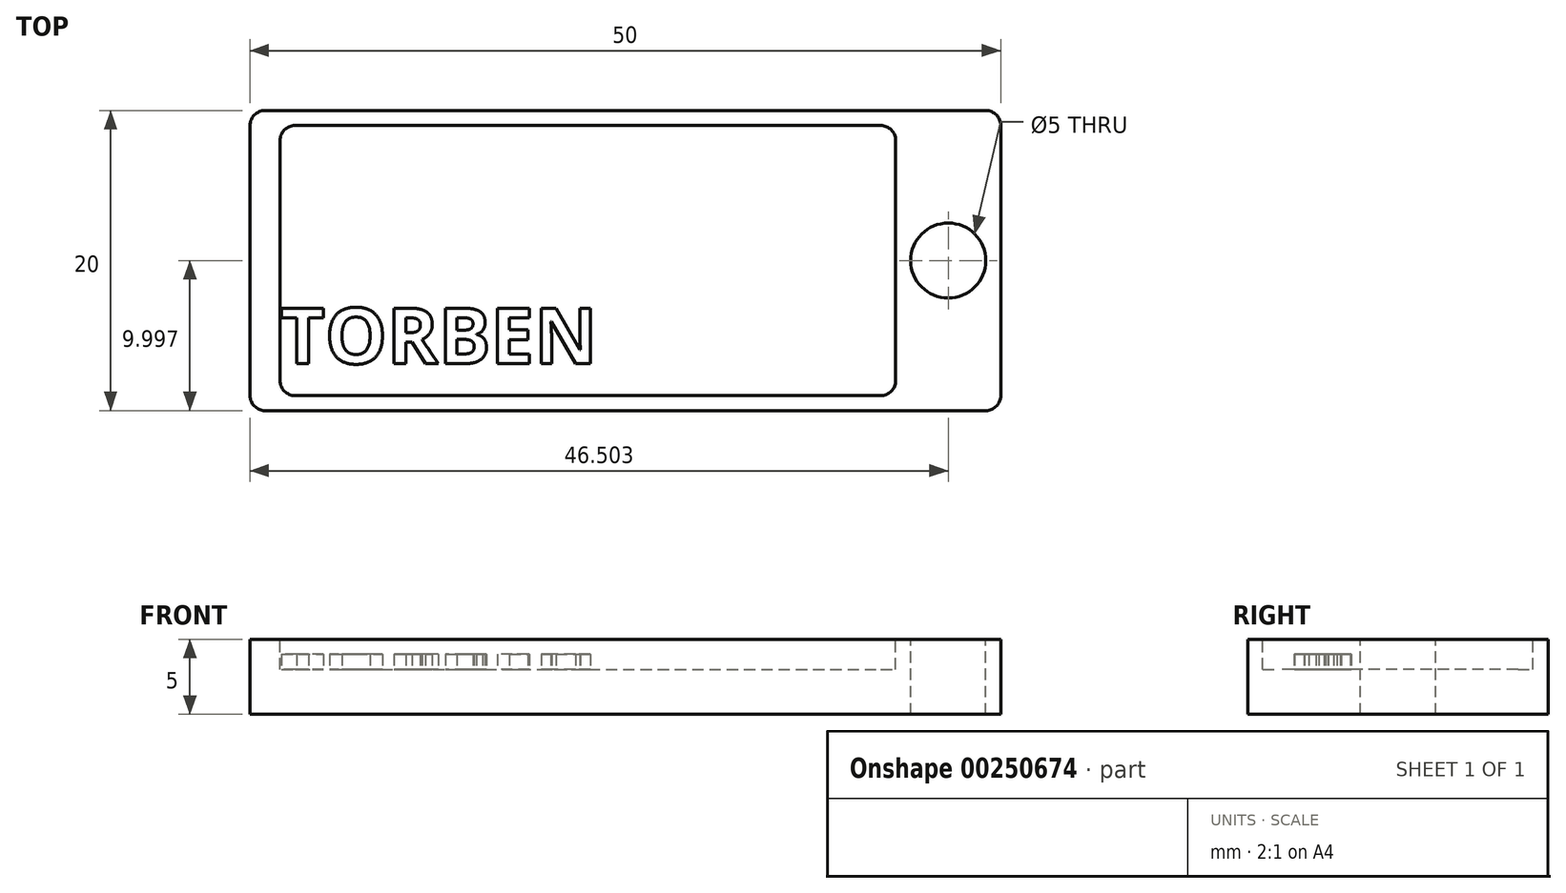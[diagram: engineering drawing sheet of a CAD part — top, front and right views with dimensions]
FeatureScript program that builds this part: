
annotation { "Feature Type Name" : "Feature", "Feature Type Description" : "" }
export const myFeature = defineFeature(function(context is Context, id is Id, definition is map)
    precondition{}
    {
        {
            var Q0;
            Q0=qCreatedBy(makeId("Top.planeOp"),FACE);
            var sketch = newSketch(context, id + "F0", { "sketchPlane" : qUnion([Q0])});
            skLineSegment(sketch, "E0.bottom", {"start": v(-8.37, 9.04) * mm, "end": v(41.63, 9.04) * mm});
            skLineSegment(sketch, "E0.top", {"start": v(-8.37, -10.96) * mm, "end": v(41.63, -10.96) * mm});
            skLineSegment(sketch, "E0.left", {"start": v(-8.37, 9.04) * mm, "end": v(-8.37, -10.96) * mm});
            skLineSegment(sketch, "E0.right", {"start": v(41.63, 9.04) * mm, "end": v(41.63, -10.96) * mm});
            skSolve(sketch);
        }
        {
            var Q0;
            Q0 = qSketchRegion(id + "F0", true);
            extrude(context, id + "F1", {"entities" : qUnion([Q0]), "depth" : 5 * mm});
        }
        {
            var Q0;
            Q0=makeQuery(id+"F1.opExtrude","CAP_FACE",FACE,{"disambiguationData":[OSD([sQuery(id+"F0.wireOp",EDGE,"E0.bottom"),sQuery(id+"F0.wireOp",EDGE,"E0.top"),sQuery(id+"F0.wireOp",EDGE,"E0.left"),sQuery(id+"F0.wireOp",EDGE,"E0.right")])],"isStart":false});
            var sketch = newSketch(context, id + "F2", { "sketchPlane" : qUnion([Q0])});
            skLineSegment(sketch, "E1.bottom", {"start": v(-6.37, 8.04) * mm, "end": v(34.63, 8.04) * mm});
            skLineSegment(sketch, "E1.top", {"start": v(-6.37, -9.96) * mm, "end": v(34.63, -9.96) * mm});
            skLineSegment(sketch, "E1.left", {"start": v(-6.37, 8.04) * mm, "end": v(-6.37, -9.96) * mm});
            skLineSegment(sketch, "E1.right", {"start": v(34.63, 8.04) * mm, "end": v(34.63, -9.96) * mm});
            skSolve(sketch);
        }
        {
            var Q0;
            Q0 = qSketchRegion(id + "F2", true);
            extrude(context, id + "F3", {"entities" : qUnion([Q0]), "operationType" : NewBodyOperationType.REMOVE, "oppositeDirection" : true, "depth" : 2 * mm});
        }
        {
            var Q0;
            Q0=makeQuery(id+"F1.opExtrude","SWEPT_EDGE",EDGE,{"disambiguationData":[OSD([sQuery(id+"F0.wireOp",EDGE,"E0.top"),sQuery(id+"F0.wireOp",EDGE,"E0.left")])]});
            var Q1;
            Q1=makeQuery(id+"F1.opExtrude","SWEPT_EDGE",EDGE,{"disambiguationData":[OSD([sQuery(id+"F0.wireOp",EDGE,"E0.bottom"),sQuery(id+"F0.wireOp",EDGE,"E0.left")])]});
            var Q2;
            Q2=makeQuery(id+"F1.opExtrude","SWEPT_EDGE",EDGE,{"disambiguationData":[OSD([sQuery(id+"F0.wireOp",EDGE,"E0.top"),sQuery(id+"F0.wireOp",EDGE,"E0.right")])]});
            var Q3;
            Q3=makeQuery(id+"F1.opExtrude","SWEPT_EDGE",EDGE,{"disambiguationData":[OSD([sQuery(id+"F0.wireOp",EDGE,"E0.bottom"),sQuery(id+"F0.wireOp",EDGE,"E0.right")])]});
            fillet(context, id + "F4", {"entities" : qUnion([Q0, Q1, Q2, Q3]), "radius" : 1 * mm, "tangentPropagation" : true, "allowEdgeOverflow" : false});
        }
        {
            var Q0;
            Q0=makeQuery(id+"F3.boolean.opBoolean","COPY",EDGE,{"derivedFrom":makeQuery(id+"F3.opExtrude","SWEPT_EDGE",EDGE,{"disambiguationData":[OSD([sQuery(id+"F2.wireOp",EDGE,"E1.bottom"),sQuery(id+"F2.wireOp",EDGE,"E1.left")])]})});
            var Q1;
            Q1=makeQuery(id+"F3.boolean.opBoolean","COPY",EDGE,{"derivedFrom":makeQuery(id+"F3.opExtrude","SWEPT_EDGE",EDGE,{"disambiguationData":[OSD([sQuery(id+"F2.wireOp",EDGE,"E1.bottom"),sQuery(id+"F2.wireOp",EDGE,"E1.right")])]})});
            var Q2;
            Q2=makeQuery(id+"F3.boolean.opBoolean","COPY",EDGE,{"derivedFrom":makeQuery(id+"F3.opExtrude","SWEPT_EDGE",EDGE,{"disambiguationData":[OSD([sQuery(id+"F2.wireOp",EDGE,"E1.top"),sQuery(id+"F2.wireOp",EDGE,"E1.left")])]})});
            var Q3;
            Q3=makeQuery(id+"F3.boolean.opBoolean","COPY",EDGE,{"derivedFrom":makeQuery(id+"F3.opExtrude","SWEPT_EDGE",EDGE,{"disambiguationData":[OSD([sQuery(id+"F2.wireOp",EDGE,"E1.top"),sQuery(id+"F2.wireOp",EDGE,"E1.right")])]})});
            fillet(context, id + "F5", {"entities" : qUnion([Q0, Q1, Q2, Q3]), "radius" : 1 * mm, "tangentPropagation" : true, "allowEdgeOverflow" : false});
        }
        {
            var Q0;
            Q0=makeQuery(id+"F1.opExtrude","CAP_FACE",FACE,{"disambiguationData":[OSD([sQuery(id+"F0.wireOp",EDGE,"E0.bottom"),sQuery(id+"F0.wireOp",EDGE,"E0.top"),sQuery(id+"F0.wireOp",EDGE,"E0.left"),sQuery(id+"F0.wireOp",EDGE,"E0.right")])],"isStart":false});
            var sketch = newSketch(context, id + "F6", { "sketchPlane" : qUnion([Q0])});
            skPoint(sketch, "E2", {"position": v(34.63, -0.96) * mm});
            skPoint(sketch, "E3", {"position": v(41.63, -0.96) * mm});
            skLineSegment(sketch, "E4", {"start": v(34.63, -0.96) * mm, "end": v(41.63, -0.96) * mm, "construction": true});
            skPoint(sketch, "E5", {"position": v(38.13, -0.96) * mm});
            skCircle(sketch, "E6", {"center": v(38.13, -0.96) * mm, "radius": 2.5 * mm});
            skSolve(sketch);
        }
        {
            var Q0;
            Q0 = qSketchRegion(id + "F6", true);
            extrude(context, id + "F7", {"entities" : qUnion([Q0]), "operationType" : NewBodyOperationType.REMOVE, "oppositeDirection" : true, "depth" : 25 * mm});
        }
        {
            var Q0;
            Q0=makeQuery(id+"F3.boolean.opBoolean","COPY",FACE,{"derivedFrom":makeQuery(id+"F3.opExtrude","CAP_FACE",FACE,{"disambiguationData":[OSD([sQuery(id+"F2.wireOp",EDGE,"E1.bottom"),sQuery(id+"F2.wireOp",EDGE,"E1.top"),sQuery(id+"F2.wireOp",EDGE,"E1.left"),sQuery(id+"F2.wireOp",EDGE,"E1.right")])],"isStart":false})});
            var sketch = newSketch(context, id + "F8", { "sketchPlane" : qUnion([Q0])});
            skText(sketch, "E7", { "text": "TORBEN", "fontName": "OpenSans-Bold.ttf"});
            skPoint(sketch, "E8", {"position": v(-6.37, -0.96) * mm});
            skPoint(sketch, "E9", {"position": v(34.63, -0.96) * mm});
            const initialGuessF8  = {"E7": [-0.00637, -0.00783, 1, 0, 0.00373]};
            skSetInitialGuess(sketch, initialGuessF8);
            skSolve(sketch);
        }
        {
            var Q0;
            Q0 = qSketchRegion(id + "F8", true);
            extrude(context, id + "F9", {"entities" : qUnion([Q0]), "operationType" : NewBodyOperationType.ADD, "depth" : 1 * mm});
        }
    });
